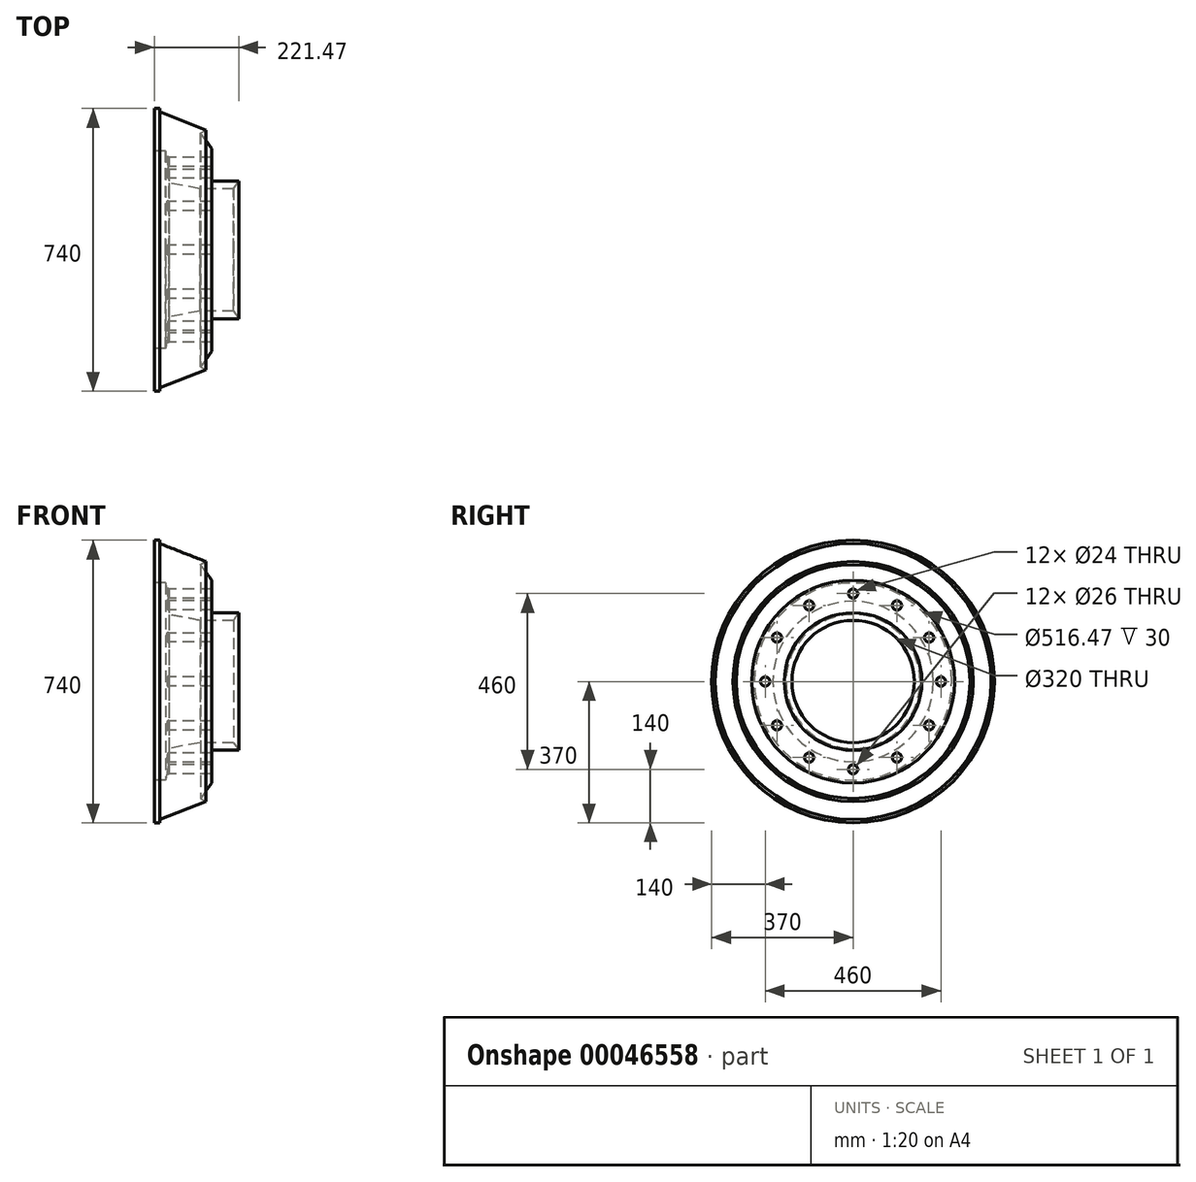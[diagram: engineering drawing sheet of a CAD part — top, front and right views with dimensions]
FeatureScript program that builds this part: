
annotation { "Feature Type Name" : "Feature", "Feature Type Description" : "" }
export const myFeature = defineFeature(function(context is Context, id is Id, definition is map)
    precondition{}
    {
        {
            var Q0;
            Q0=qCreatedBy(makeId("Front.planeOp"),FACE);
            var sketch = newSketch(context, id + "F0", { "sketchPlane" : qUnion([Q0])});
            skLineSegment(sketch, "E0", {"start": v(-182.35, 85.52) * mm, "end": v(-182.35, 0) * mm});
            skLineSegment(sketch, "E1", {"start": v(-182.35, 0) * mm, "end": v(-166.35, 0) * mm});
            skLineSegment(sketch, "E2", {"start": v(-182.35, 85.52) * mm, "end": v(-211.5, 126.14) * mm});
            skLineSegment(sketch, "E3", {"start": v(-211.5, 126.14) * mm, "end": v(-197.55, 133.96) * mm});
            skLineSegment(sketch, "E4", {"start": v(-124.76, -20) * mm, "end": v(-110.88, 0) * mm});
            skLineSegment(sketch, "E5", {"start": v(-110.88, 0) * mm, "end": v(-182.35, 0) * mm});
            skLineSegment(sketch, "E6", {"start": v(-197.55, 133.96) * mm, "end": v(-318.6, 181.36) * mm});
            skLineSegment(sketch, "E7", {"start": v(-293.75, -4.67) * mm, "end": v(-293.75, 30) * mm});
            skPoint(sketch, "E8.start.orphan", {"position": v(-318.6, 190) * mm});
            skLineSegment(sketch, "E9", {"start": v(-318.6, 181.36) * mm, "end": v(-318.6, 190) * mm});
            skLineSegment(sketch, "E10", {"start": v(-332.35, 181.7) * mm, "end": v(-332.35, 190) * mm});
            skLineSegment(sketch, "E11", {"start": v(-332.35, 190) * mm, "end": v(-318.6, 190) * mm});
            skLineSegment(sketch, "E12", {"start": v(-124.76, -20) * mm, "end": v(-213.14, -20) * mm});
            skLineSegment(sketch, "E13", {"start": v(-213.14, -20) * mm, "end": v(-293.75, -4.67) * mm});
            skLineSegment(sketch, "E14", {"start": v(-332.35, 181.7) * mm, "end": v(-332.35, 78.23) * mm});
            skLineSegment(sketch, "E15", {"start": v(-332.35, 78.23) * mm, "end": v(-302.35, 78.23) * mm});
            skLineSegment(sketch, "E16", {"start": v(-293.75, 30) * mm, "end": v(-302.35, 78.23) * mm});
            skLineSegment(sketch, "E17", {"start": v(-315.68, -180) * mm, "end": v(53.16, -180) * mm, "construction": true});
            skSolve(sketch);
        }
        {
            var Q0;
            {var subQ2=sQuery(id+"F0.wireOp",EDGE,"E0");Q0=makeQuery(id+"F0.imprint","IMPRINT",FACE,{"disambiguationData":[TD([[makeQuery(id+"F0.imprint","IMPRINT",EDGE,{"derivedFrom":subQ2}),-1.0]])]});}
            var Q1;
            Q1=sQuery(id+"F0.wireOp",EDGE,"E17");
            revolve(context, id + "F1", {"entities" : qUnion([Q0]), "axis" : qUnion([Q1]), "revolveType" : RevolveType.FULL});
        }
        {
            var Q0;
            Q0=makeQuery(id+"F1.opRevolve","SWEPT_FACE",FACE,{"disambiguationData":[OSD([sQuery(id+"F0.wireOp",EDGE,"E10"),sQuery(id+"F0.wireOp",EDGE,"E14")])]});
            var sketch = newSketch(context, id + "F2", { "sketchPlane" : qUnion([Q0])});
            skCircle(sketch, "E18", {"center": v(0, -180) * mm, "radius": 230 * mm});
            skCircle(sketch, "E19", {"center": v(0, 50) * mm, "radius": 12 * mm});
            skCircle(sketch, "E20.1.0", {"center": v(-115, 19.19) * mm, "radius": 12 * mm});
            skCircle(sketch, "E20.2.0", {"center": v(-199.19, -65) * mm, "radius": 12 * mm});
            skCircle(sketch, "E21.1.3.0", {"center": v(-230, -180) * mm, "radius": 12 * mm});
            skCircle(sketch, "E21.1.4.0", {"center": v(-199.19, -295) * mm, "radius": 12 * mm});
            skCircle(sketch, "E21.1.5.0", {"center": v(-115, -379.19) * mm, "radius": 12 * mm});
            skCircle(sketch, "E21.1.6.0", {"center": v(0, -410) * mm, "radius": 12 * mm});
            skCircle(sketch, "E21.1.7.0", {"center": v(115, -379.19) * mm, "radius": 12 * mm});
            skCircle(sketch, "E21.1.8.0", {"center": v(199.19, -295) * mm, "radius": 12 * mm});
            skCircle(sketch, "E21.1.9.0", {"center": v(230, -180) * mm, "radius": 12 * mm});
            skCircle(sketch, "E21.1.10.0", {"center": v(199.19, -65) * mm, "radius": 12 * mm});
            skCircle(sketch, "E21.1.11.0", {"center": v(115, 19.19) * mm, "radius": 12 * mm});
            skSolve(sketch);
        }
        {
            var Q0;
            Q0=sQuery(id+"F2.wireOp",VERTEX,"E19.center");
            var Q1;
            Q1=sQuery(id+"F2.wireOp",VERTEX,"E21.1.11.0.center");
            var Q2;
            Q2=sQuery(id+"F2.wireOp",VERTEX,"E21.1.10.0.center");
            var Q3;
            Q3=sQuery(id+"F2.wireOp",VERTEX,"E21.1.9.0.center");
            var Q4;
            Q4=sQuery(id+"F2.wireOp",VERTEX,"E21.1.8.0.center");
            var Q5;
            Q5=sQuery(id+"F2.wireOp",VERTEX,"E21.1.7.0.center");
            var Q6;
            Q6=sQuery(id+"F2.wireOp",VERTEX,"E21.1.6.0.center");
            var Q7;
            Q7=sQuery(id+"F2.wireOp",VERTEX,"E21.1.5.0.center");
            var Q8;
            Q8=sQuery(id+"F2.wireOp",VERTEX,"E21.1.4.0.center");
            var Q9;
            Q9=sQuery(id+"F2.wireOp",VERTEX,"E21.1.3.0.center");
            var Q10;
            Q10=sQuery(id+"F2.wireOp",VERTEX,"E20.2.0.center");
            var Q11;
            Q11=sQuery(id+"F2.wireOp",VERTEX,"E20.1.0.center");
            var Q12;
            Q12=makeQuery(id+"F1.opRevolve","SWEPT_BODY",BODY,{"disambiguationData":[OSD([sQuery(id+"F0.wireOp",EDGE,"E0"),sQuery(id+"F0.wireOp",EDGE,"E2"),sQuery(id+"F0.wireOp",EDGE,"E3"),sQuery(id+"F0.wireOp",EDGE,"E4"),sQuery(id+"F0.wireOp",EDGE,"E5"),sQuery(id+"F0.wireOp",EDGE,"E6"),sQuery(id+"F0.wireOp",EDGE,"E7"),sQuery(id+"F0.wireOp",EDGE,"E9"),sQuery(id+"F0.wireOp",EDGE,"E10"),sQuery(id+"F0.wireOp",EDGE,"E11"),sQuery(id+"F0.wireOp",EDGE,"E12"),sQuery(id+"F0.wireOp",EDGE,"E13"),sQuery(id+"F0.wireOp",EDGE,"E14"),sQuery(id+"F0.wireOp",EDGE,"E15"),sQuery(id+"F0.wireOp",EDGE,"E16")])]});
            hole(context, id + "F3", {"style" : HoleStyle.C_SINK, "holeDiameter" : 24 * mm, "cSinkDiameter" : 26 * mm, "endStyle" : HoleEndStyle.BLIND, "holeDepth" : 300 * mm, "locations" : qUnion([Q0, Q1, Q2, Q3, Q4, Q5, Q6, Q7, Q8, Q9, Q10, Q11]), "scope" : qUnion([Q12]), "cSinkAngle" : 90 * degree});
        }
    });
